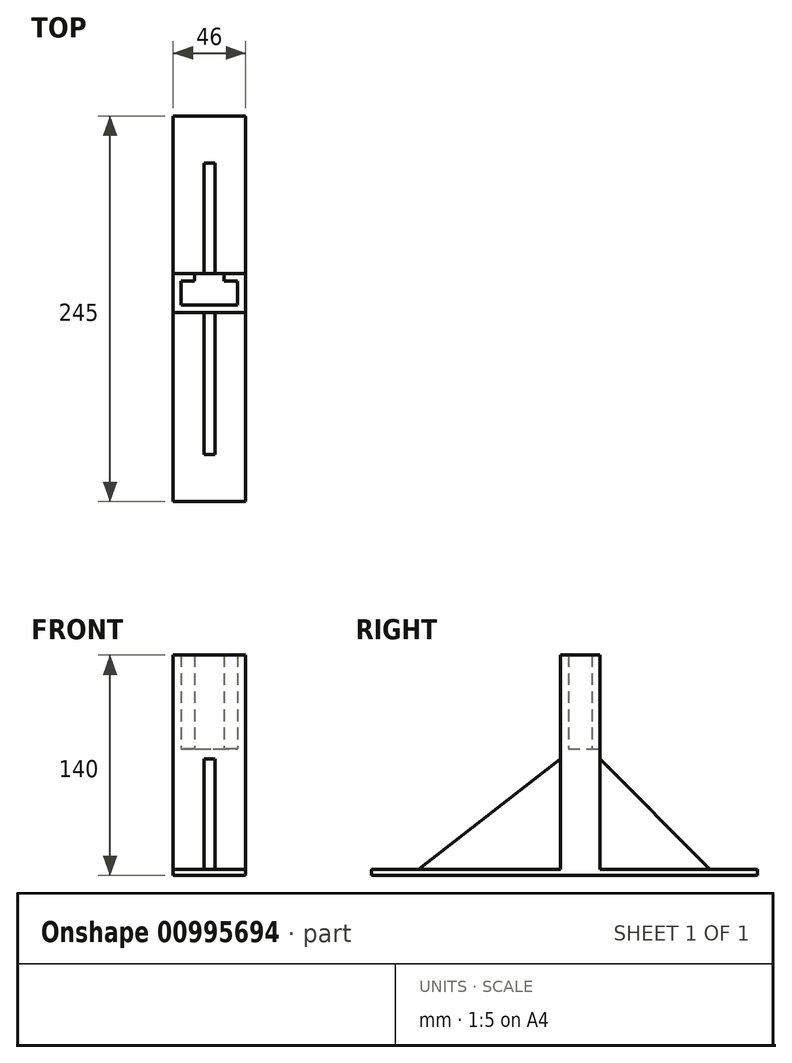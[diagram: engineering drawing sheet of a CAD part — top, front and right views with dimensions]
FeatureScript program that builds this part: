
annotation { "Feature Type Name" : "Feature", "Feature Type Description" : "" }
export const myFeature = defineFeature(function(context is Context, id is Id, definition is map)
    precondition{}
    {
        {
            var Q0;
            Q0=qCreatedBy(makeId("Front.planeOp"),FACE);
            var sketch = newSketch(context, id + "F0", { "sketchPlane" : qUnion([Q0])});
            skLineSegment(sketch, "E0.bottom", {"start": v(-35.47, 8.44) * mm, "end": v(10.53, 8.44) * mm});
            skLineSegment(sketch, "E0.top", {"start": v(-35.47, -71.56) * mm, "end": v(10.53, -71.56) * mm});
            skLineSegment(sketch, "E0.left", {"start": v(-35.47, 8.44) * mm, "end": v(-35.47, -71.56) * mm});
            skLineSegment(sketch, "E0.right", {"start": v(10.53, 8.44) * mm, "end": v(10.53, -71.56) * mm});
            skSolve(sketch);
        }
        {
            var Q0;
            Q0=makeQuery(id+"F0.imprint","IMPRINT",FACE,{"disambiguationData":[TD([[makeQuery(id+"F0.imprint","IMPRINT",EDGE,{"derivedFrom":sQuery(id+"F0.wireOp",EDGE,"E0.bottom")}),-1.0]])]});
            extrude(context, id + "F1", {"entities" : qUnion([Q0]), "depth" : 25 * mm, "offsetDistance" : 25 * mm});
        }
        {
            var Q0;
            Q0=makeQuery(id+"F1.opExtrude","SWEPT_FACE",FACE,{"disambiguationData":[OSD([sQuery(id+"F0.wireOp",EDGE,"E0.left")])]});
            var sketch = newSketch(context, id + "F2", { "sketchPlane" : qUnion([Q0])});
            skLineSegment(sketch, "E1", {"start": v(0, -71.56) * mm, "end": v(-100, -71.56) * mm});
            skLineSegment(sketch, "E2", {"start": v(-100, -71.56) * mm, "end": v(-100, -67.56) * mm});
            skLineSegment(sketch, "E3", {"start": v(-100, -67.56) * mm, "end": v(0, -67.56) * mm});
            skLineSegment(sketch, "E4", {"start": v(-70, -67.56) * mm, "end": v(0, 2.44) * mm});
            skLineSegment(sketch, "E5", {"start": v(25, -71.56) * mm, "end": v(145, -71.56) * mm});
            skLineSegment(sketch, "E6", {"start": v(145, -71.56) * mm, "end": v(145, -67.56) * mm});
            skLineSegment(sketch, "E7", {"start": v(145, -67.56) * mm, "end": v(25, -67.56) * mm});
            skLineSegment(sketch, "E8", {"start": v(25, 2.44) * mm, "end": v(115, -67.56) * mm});
            skSolve(sketch);
        }
        {
            var Q0;
            Q0=makeQuery(id+"F1.opExtrude","SWEPT_FACE",FACE,{"disambiguationData":[OSD([sQuery(id+"F0.wireOp",EDGE,"E0.bottom")])]});
            var sketch = newSketch(context, id + "F3", { "sketchPlane" : qUnion([Q0])});
            skLineSegment(sketch, "E9.0.0", {"start": v(10.53, 0) * mm, "end": v(-35.47, 0) * mm});
            skLineSegment(sketch, "E9.0.1", {"start": v(-35.47, 0) * mm, "end": v(-35.47, -25) * mm});
            skLineSegment(sketch, "E9.0.2", {"start": v(-35.47, -25) * mm, "end": v(10.53, -25) * mm});
            skLineSegment(sketch, "E9.0.3", {"start": v(10.53, -25) * mm, "end": v(10.53, 0) * mm});
            skLineSegment(sketch, "E10.0", {"start": v(5.53, -5) * mm, "end": v(-30.47, -5) * mm});
            skLineSegment(sketch, "E10.1", {"start": v(5.53, -20) * mm, "end": v(5.53, -5) * mm});
            skLineSegment(sketch, "E10.2", {"start": v(-30.47, -20) * mm, "end": v(5.53, -20) * mm});
            skLineSegment(sketch, "E10.3", {"start": v(-30.47, -5) * mm, "end": v(-30.47, -20) * mm});
            skPoint(sketch, "E11", {"position": v(-21.72, -5) * mm});
            skPoint(sketch, "E12", {"position": v(-3.22, -5) * mm});
            skLineSegment(sketch, "E13", {"start": v(-21.72, -5) * mm, "end": v(-21.72, 0) * mm});
            skLineSegment(sketch, "E14", {"start": v(-3.22, -5) * mm, "end": v(-3.22, 0) * mm});
            skPoint(sketch, "E15", {"position": v(-12.47, -5) * mm});
            skSolve(sketch);
        }
        {
            var Q0;
            {var subQ6=sQuery(id+"F3.wireOp",EDGE,"E9.0.1");Q0=makeQuery(id+"F3.imprint","IMPRINT",FACE,{"disambiguationData":[TD([[makeQuery(id+"F3.imprint","IMPRINT",EDGE,{"derivedFrom":subQ6}),-1.0]])]});}
            extrude(context, id + "F4", {"entities" : qUnion([Q0]), "operationType" : NewBodyOperationType.ADD, "depth" : 60 * mm, "offsetDistance" : 25 * mm});
        }
        {
            var Q0;
            {var subQ6=sQuery(id+"F2.wireOp",EDGE,"E1");Q0=makeQuery(id+"F2.imprint","IMPRINT",FACE,{"disambiguationData":[TD([[makeQuery(id+"F2.imprint","IMPRINT",EDGE,{"derivedFrom":subQ6}),-1.0]])]});}
            var Q1;
            {var subQ6=sQuery(id+"F2.wireOp",EDGE,"E5");Q1=makeQuery(id+"F2.imprint","IMPRINT",FACE,{"disambiguationData":[TD([[makeQuery(id+"F2.imprint","IMPRINT",EDGE,{"derivedFrom":subQ6}),1.0]])]});}
            extrude(context, id + "F5", {"entities" : qUnion([Q0, Q1]), "operationType" : NewBodyOperationType.ADD, "oppositeDirection" : true, "depth" : 46 * mm, "offsetDistance" : 25 * mm});
        }
        {
            var Q0;
            {var subQ0=sQuery(id+"F0.wireOp",EDGE,"E0.left");Q0=makeQuery(id+"F5.boolean.opBoolean","MERGE",FACE,{"derivedFrom":[makeQuery(id+"F4.boolean.opBoolean","MERGE",FACE,{"derivedFrom":[makeQuery(id+"F1.opExtrude","SWEPT_FACE",FACE,{"disambiguationData":[OSD([subQ0])]}),makeQuery(id+"F4.opExtrude","SWEPT_FACE",FACE,{"disambiguationData":[OSD([sQuery(id+"F3.wireOp",EDGE,"E9.0.1")])]})]}),makeQuery(id+"F5.opExtrude","CAP_FACE",FACE,{"disambiguationData":[OSD([subQ0,sQuery(id+"F2.wireOp",EDGE,"E1"),sQuery(id+"F2.wireOp",EDGE,"E2"),sQuery(id+"F2.wireOp",EDGE,"E3")])],"isStart":true}),makeQuery(id+"F5.opExtrude","CAP_FACE",FACE,{"disambiguationData":[OSD([subQ0,sQuery(id+"F2.wireOp",EDGE,"E5"),sQuery(id+"F2.wireOp",EDGE,"E6"),sQuery(id+"F2.wireOp",EDGE,"E7")])],"isStart":true})]});}
            cPlane(context, id + "F6", {"entities" : qUnion([Q0]), "cplaneType" : CPlaneType.OFFSET, "offset" : 23 * mm, "oppositeDirection" : true, "width" : 150 * mm, "height" : 150 * mm});
        }
        {
            var Q0;
            Q0=qCreatedBy(id+"F6.planeOp",FACE);
            var sketch = newSketch(context, id + "F7", { "sketchPlane" : qUnion([Q0])});
            skLineSegment(sketch, "E16.0.0", {"start": v(0, 68.44) * mm, "end": v(0, -67.56) * mm});
            skLineSegment(sketch, "E16.0.2", {"start": v(0, -67.56) * mm, "end": v(0, 68.44) * mm});
            skLineSegment(sketch, "E16.0.4", {"start": v(0, 68.44) * mm, "end": v(0, 8.44) * mm});
            skLineSegment(sketch, "E16.0.6", {"start": v(0, 8.44) * mm, "end": v(0, 68.44) * mm});
            skLineSegment(sketch, "E17", {"start": v(0, -67.56) * mm, "end": v(-70, -67.56) * mm});
            skLineSegment(sketch, "E18", {"start": v(-70, -67.56) * mm, "end": v(0, 2.44) * mm});
            skLineSegment(sketch, "E19.0.1", {"start": v(25, -67.56) * mm, "end": v(25, 68.44) * mm});
            skLineSegment(sketch, "E19.0.3", {"start": v(25, 68.44) * mm, "end": v(25, -67.56) * mm});
            skLineSegment(sketch, "E20", {"start": v(25, -67.56) * mm, "end": v(115, -67.56) * mm});
            skLineSegment(sketch, "E21", {"start": v(115, -67.56) * mm, "end": v(25, 2.44) * mm});
            skSolve(sketch);
        }
        {
            var Q0;
            {var subQ0=sQuery(id+"F7.wireOp",EDGE,"E17");Q0=makeQuery(id+"F7.imprint","IMPRINT",FACE,{"disambiguationData":[TD([[makeQuery(id+"F7.imprint","IMPRINT",EDGE,{"derivedFrom":subQ0}),-1.0]])]});}
            var Q1;
            {var subQ0=sQuery(id+"F7.wireOp",EDGE,"E20");Q1=makeQuery(id+"F7.imprint","IMPRINT",FACE,{"disambiguationData":[TD([[makeQuery(id+"F7.imprint","IMPRINT",EDGE,{"derivedFrom":subQ0}),1.0]])]});}
            extrude(context, id + "F8", {"entities" : qUnion([Q0, Q1]), "operationType" : NewBodyOperationType.ADD, "endBound" : BoundingType.SYMMETRIC, "depth" : 7 * mm, "offsetDistance" : 25 * mm});
        }
        {
            var Q0;
            {var subQ0=sQuery(id+"F3.wireOp",EDGE,"E9.0.0");Q0=makeQuery(id+"F4.boolean.opBoolean","MERGE",FACE,{"derivedFrom":[makeQuery(id+"F1.opExtrude","CAP_FACE",FACE,{"disambiguationData":[OSD([sQuery(id+"F0.wireOp",EDGE,"E0.bottom"),sQuery(id+"F0.wireOp",EDGE,"E0.top"),sQuery(id+"F0.wireOp",EDGE,"E0.left"),sQuery(id+"F0.wireOp",EDGE,"E0.right")])],"isStart":true}),makeQuery(id+"F4.opExtrude","SWEPT_FACE",FACE,{"disambiguationData":[OSD([subQ0]),TDD([makeQuery(id+"F3.imprint","IMPRINT",EDGE,{"disambiguationData":[TD([[makeQuery(id+"F3.imprint","INTERSECT",VERTEX,{"derivedFrom":[subQ0,sQuery(id+"F3.wireOp",EDGE,"E9.0.1")]}),-1.0]])],"derivedFrom":subQ0})])]}),makeQuery(id+"F4.opExtrude","SWEPT_FACE",FACE,{"disambiguationData":[OSD([subQ0]),TDD([makeQuery(id+"F3.imprint","IMPRINT",EDGE,{"disambiguationData":[TD([[makeQuery(id+"F3.imprint","INTERSECT",VERTEX,{"derivedFrom":[subQ0,sQuery(id+"F3.wireOp",EDGE,"E9.0.3")]}),1.0]])],"derivedFrom":subQ0})])]})]});}
            var sketch = newSketch(context, id + "F9", { "sketchPlane" : qUnion([Q0])});
            skLineSegment(sketch, "E22", {"start": v(21.72, 8.84) * mm, "end": v(21.72, -71.56) * mm});
            skSolve(sketch);
        }
        {
            var Q0;
            Q0=makeQuery(id+"F1.opExtrude","SWEPT_FACE",FACE,{"disambiguationData":[OSD([sQuery(id+"F0.wireOp",EDGE,"E0.bottom")])]});
            var Q1;
            Q1=sQuery(id+"F9.wireOp",VERTEX,"E22.start");
            extrude(context, id + "F10", {"entities" : qUnion([Q0]), "operationType" : NewBodyOperationType.ADD, "endBound" : BoundingType.UP_TO_VERTEX, "depth" : 2.2 * mm, "endBoundEntityVertex" : qUnion([Q1]), "offsetDistance" : 25 * mm});
        }
    });
